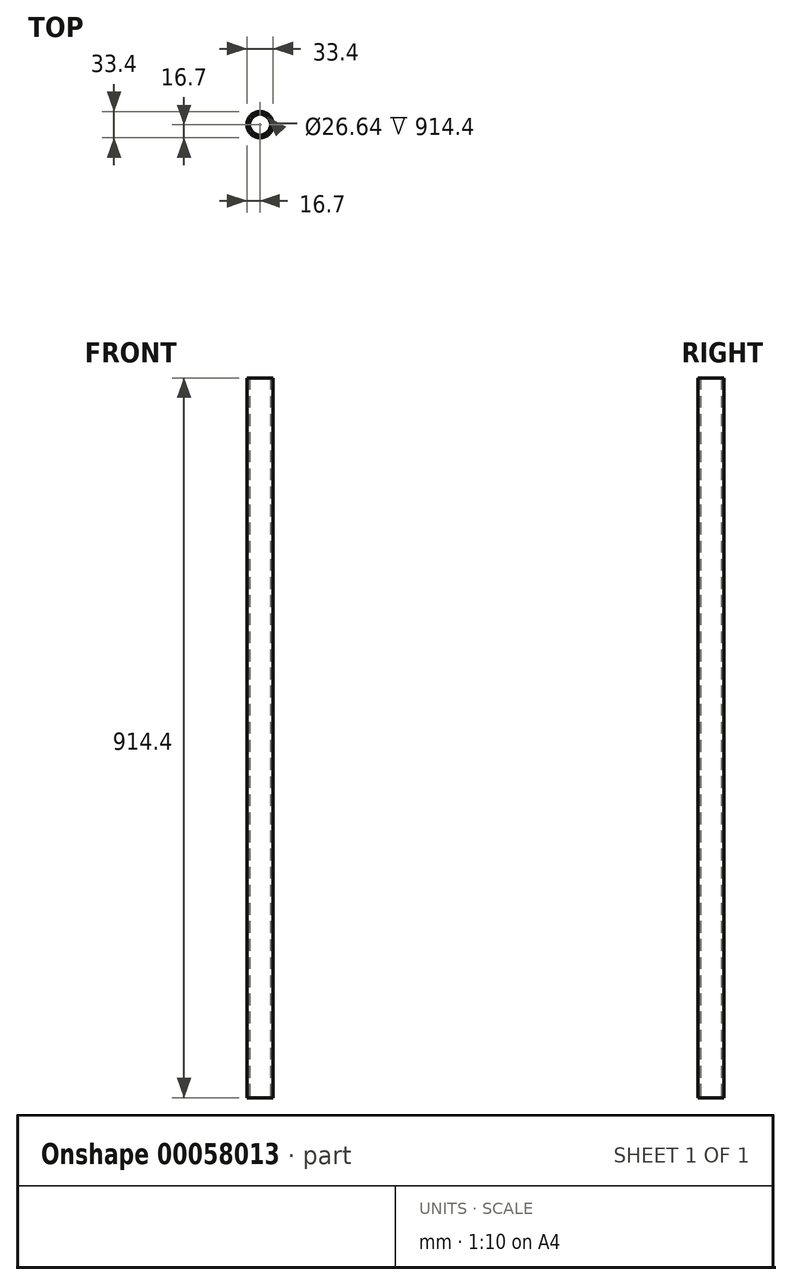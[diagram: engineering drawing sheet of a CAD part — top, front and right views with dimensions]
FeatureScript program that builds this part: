
annotation { "Feature Type Name" : "Feature", "Feature Type Description" : "" }
export const myFeature = defineFeature(function(context is Context, id is Id, definition is map)
    precondition{}
    {
        {
            var Q0;
            Q0=qCreatedBy(makeId("Top.planeOp"),FACE);
            var sketch = newSketch(context, id + "F0", { "sketchPlane" : qUnion([Q0])});
            skCircle(sketch, "E0", {"center": v(0, 0) * mm, "radius": 16.7 * mm});
            skCircle(sketch, "E1", {"center": v(0, 0) * mm, "radius": 13.32 * mm});
            skSolve(sketch);
        }
        {
            var Q0;
            Q0=qSketchRegion(id+"F0",true);
            extrude(context, id + "F1", {"entities" : qUnion([Q0]), "depth" : 914.4 * mm});
        }
    });
